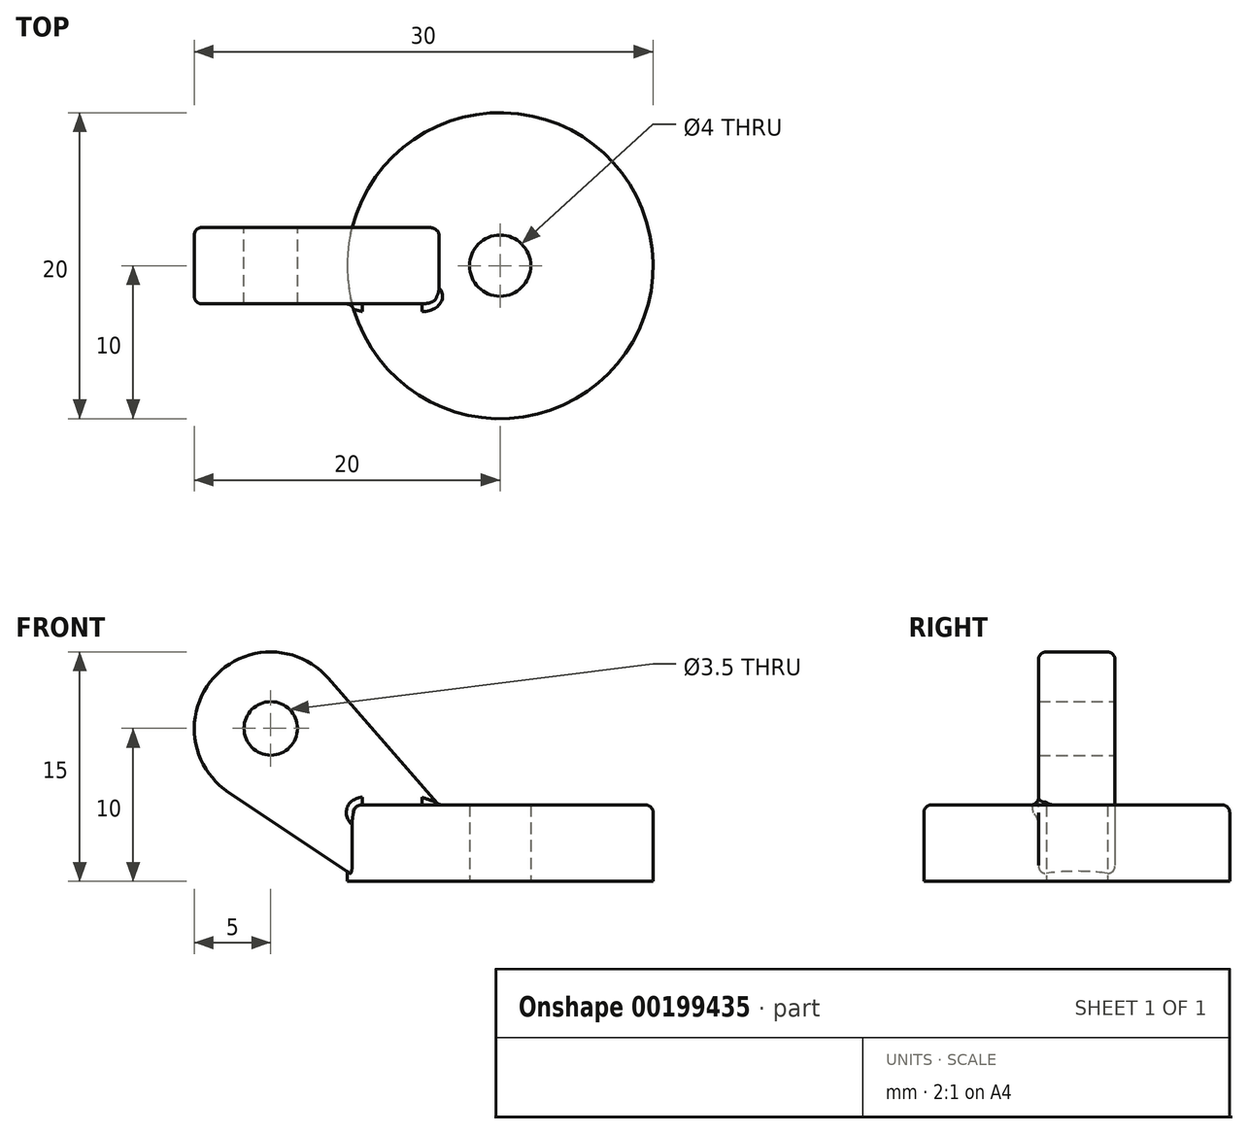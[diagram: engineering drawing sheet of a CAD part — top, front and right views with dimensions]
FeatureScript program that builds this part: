
annotation { "Feature Type Name" : "Feature", "Feature Type Description" : "" }
export const myFeature = defineFeature(function(context is Context, id is Id, definition is map)
    precondition{}
    {
        {
            var Q0;
            Q0=qCreatedBy(makeId("Top.planeOp"),FACE);
            var sketch = newSketch(context, id + "F0", { "sketchPlane" : qUnion([Q0])});
            skCircle(sketch, "E0", {"center": v(0, 0) * mm, "radius": 10 * mm});
            skCircle(sketch, "E1", {"center": v(0, 0) * mm, "radius": 2 * mm});
            skSolve(sketch);
        }
        {
            var Q0;
            Q0 = qSketchRegion(id + "F0", true);
            extrude(context, id + "F1", {"entities" : qUnion([Q0]), "depth" : 5 * mm});
        }
        {
            var Q0;
            Q0=qCreatedBy(makeId("Front.planeOp"),FACE);
            var sketch = newSketch(context, id + "F2", { "sketchPlane" : qUnion([Q0])});
            skLineSegment(sketch, "E2", {"start": v(-4, 5) * mm, "end": v(-15, 5) * mm});
            skCircle(sketch, "E3", {"center": v(-15, 10) * mm, "radius": 5 * mm});
            skLineSegment(sketch, "E4", {"start": v(0, 4.88) * mm, "end": v(0, 16.22) * mm, "construction": true});
            skLineSegment(sketch, "E5", {"start": v(-4, 5) * mm, "end": v(-11.23, 13.29) * mm});
            skCircle(sketch, "E6", {"center": v(-15, 10) * mm, "radius": 1.75 * mm});
            skLineSegment(sketch, "E7", {"start": v(-17.77, 5.84) * mm, "end": v(-9, 0) * mm});
            skLineSegment(sketch, "E8", {"start": v(-9, 0) * mm, "end": v(-4, 5) * mm});
            skSolve(sketch);
        }
        {
            var Q0;
            Q0 = qSketchRegion(id + "F2", true);
            extrude(context, id + "F3", {"entities" : qUnion([Q0]), "operationType" : NewBodyOperationType.ADD, "endBound" : BoundingType.SYMMETRIC, "depth" : 5 * mm});
        }
        {
            var Q0;
            Q0=makeQuery(id+"F1.opExtrude","CAP_EDGE",EDGE,{"disambiguationData":[OSD([sQuery(id+"F0.wireOp",EDGE,"E0")])],"isStart":false});
            var Q1;
            Q1=makeQuery(id+"F3.opExtrude","CAP_EDGE",EDGE,{"disambiguationData":[OSD([sQuery(id+"F2.wireOp",EDGE,"E5")])],"isStart":false});
            var Q2;
            Q2=makeQuery(id+"F3.opExtrude","CAP_EDGE",EDGE,{"disambiguationData":[OSD([sQuery(id+"F2.wireOp",EDGE,"E5")])],"isStart":true});
            var Q3;
            Q3=makeQuery(id+"F3.boolean.opBoolean","INTERSECT",EDGE,{"derivedFrom":[makeQuery(id+"F1.opExtrude","CAP_FACE",FACE,{"disambiguationData":[OSD([sQuery(id+"F0.wireOp",EDGE,"E0"),sQuery(id+"F0.wireOp",EDGE,"E1")])],"isStart":false}),makeQuery(id+"F3.opExtrude","CAP_FACE",FACE,{"disambiguationData":[OSD([sQuery(id+"F2.wireOp",EDGE,"E3"),sQuery(id+"F2.wireOp",EDGE,"E5"),sQuery(id+"F2.wireOp",EDGE,"E6"),sQuery(id+"F2.wireOp",EDGE,"E7"),sQuery(id+"F2.wireOp",EDGE,"E8")])],"isStart":false})]});
            fillet(context, id + "F4", {"entities" : qUnion([Q0, Q1, Q2, Q3]), "radius" : 0.5 * mm, "tangentPropagation" : true, "allowEdgeOverflow" : false});
        }
    });
